# Revit family: Furniture_Other-Furniture_Midmark_Wall-Hung-Full-Tall-Cabinetry__
name_source: partatom
category: Casework
units: mm (PartAtom-declared; Revit-internal decimal feet)

## family parameters
Cut with Voids When Loaded = No
Host = Face
Room Calculation Point = No
Shared = No

## types (1)
- Default - Please Load Revit Family Type Catalog
    Cabinet Finish = Wood - Midmark - Storm
    Default Elevation = 6' - 3"
    Depth = 1' - 6"
    Description = Synthesis Cabinetry provides maximum flexibility with configurable options to meet your needs—for today and tomorrow. Sterilization towers, lab towers and wall-hung tall cabinets can be configured for access from seated or standing positions, while offering better ergonomic support.
    Door Drawer Configuration = Door Drawer Options : RH Door
    Glass Panel = Glass - Midmark - Frosted
    Height = 5' - 7"
    Manufacturer = Midmark
    Model = TE01 - RH Door - 24x67
    Product Guid = d7e7c08d-e4eb-482a-a033-29daa7809f8e
    Product Page URL = https://www.midmark.com
    Product data url = https://www.bimobject.com
    URL = https://www.midmark.com
    Width = 2' - 0"
    z_Height Doorhandle = 2' - 9 1/2"

## geometry (parser evidence)
native form markers: Sweep x6
no freeform markers — native parametric forms only
